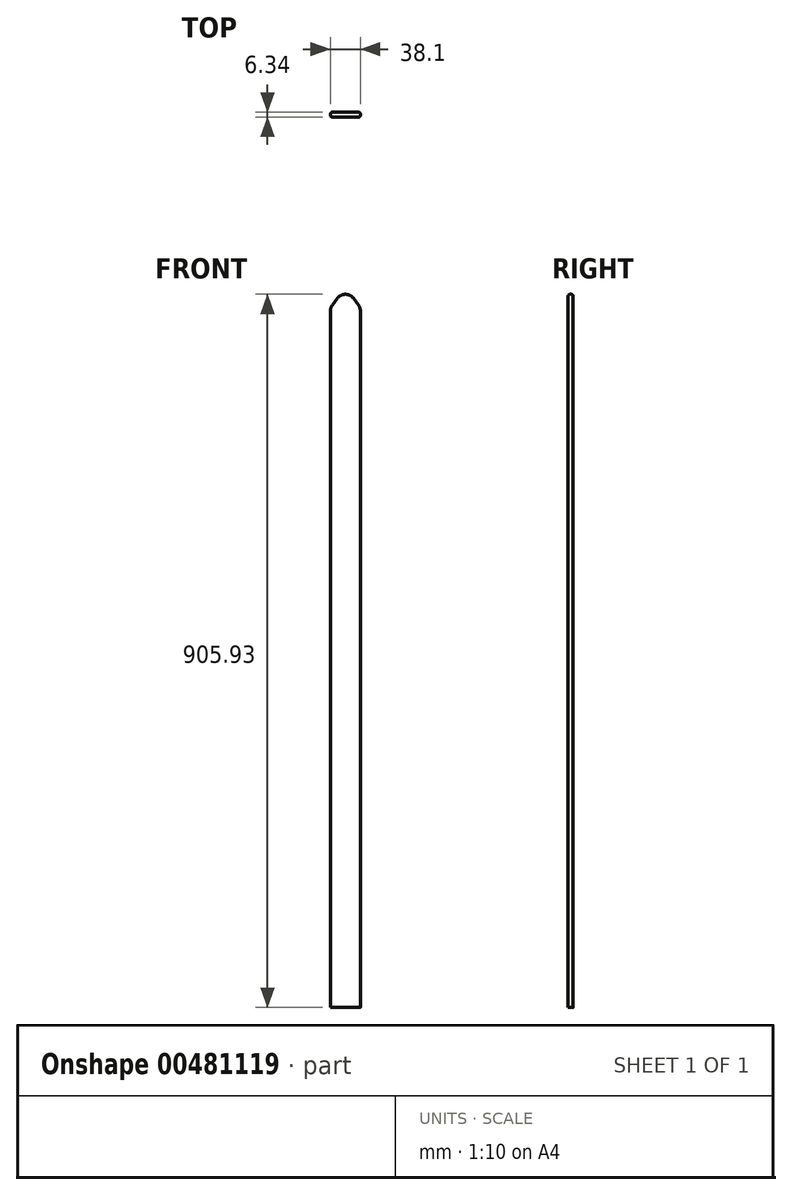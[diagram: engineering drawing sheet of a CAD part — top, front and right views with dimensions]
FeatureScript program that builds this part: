
annotation { "Feature Type Name" : "Feature", "Feature Type Description" : "" }
export const myFeature = defineFeature(function(context is Context, id is Id, definition is map)
    precondition{}
    {
        {
            var Q0;
            Q0=qCreatedBy(makeId("Front.planeOp"),FACE);
            var sketch = newSketch(context, id + "F0", { "sketchPlane" : qUnion([Q0])});
            skLineSegment(sketch, "E0", {"start": v(-19.05, 0) * mm, "end": v(-19.05, 889) * mm});
            skLineSegment(sketch, "E1", {"start": v(-19.05, 889) * mm, "end": v(0, 914.4) * mm});
            skLineSegment(sketch, "E2", {"start": v(0, 0) * mm, "end": v(0, 669.35) * mm, "construction": true});
            skLineSegment(sketch, "E3.MirrorCS", {"start": v(19.05, 889) * mm, "end": v(0, 914.4) * mm});
            skLineSegment(sketch, "E4.MirrorCS", {"start": v(19.05, 0) * mm, "end": v(19.05, 889) * mm});
            skLineSegment(sketch, "E5", {"start": v(-19.05, 0) * mm, "end": v(19.05, 0) * mm});
            skSolve(sketch);
        }
        {
            var Q0;
            Q0 = qSketchRegion(id + "F0", true);
            extrude(context, id + "F1", {"entities" : qUnion([Q0]), "endBound" : BoundingType.SYMMETRIC, "depth" : 6.35 * mm});
        }
        {
            var Q0;
            Q0=makeQuery(id+"F1.opExtrude","CAP_EDGE",EDGE,{"disambiguationData":[OSD([sQuery(id+"F0.wireOp",EDGE,"E0")])],"isStart":false});
            var Q1;
            Q1=makeQuery(id+"F1.opExtrude","CAP_EDGE",EDGE,{"disambiguationData":[OSD([sQuery(id+"F0.wireOp",EDGE,"E0")])],"isStart":true});
            var Q2;
            Q2=makeQuery(id+"F1.opExtrude","CAP_EDGE",EDGE,{"disambiguationData":[OSD([sQuery(id+"F0.wireOp",EDGE,"E1")])],"isStart":false});
            var Q3;
            Q3=makeQuery(id+"F1.opExtrude","CAP_EDGE",EDGE,{"disambiguationData":[OSD([sQuery(id+"F0.wireOp",EDGE,"E3.MirrorCS")])],"isStart":false});
            var Q4;
            Q4=makeQuery(id+"F1.opExtrude","CAP_EDGE",EDGE,{"disambiguationData":[OSD([sQuery(id+"F0.wireOp",EDGE,"E4.MirrorCS")])],"isStart":false});
            var Q5;
            Q5=makeQuery(id+"F1.opExtrude","CAP_EDGE",EDGE,{"disambiguationData":[OSD([sQuery(id+"F0.wireOp",EDGE,"E4.MirrorCS")])],"isStart":true});
            var Q6;
            Q6=makeQuery(id+"F1.opExtrude","CAP_EDGE",EDGE,{"disambiguationData":[OSD([sQuery(id+"F0.wireOp",EDGE,"E3.MirrorCS")])],"isStart":true});
            var Q7;
            Q7=makeQuery(id+"F1.opExtrude","CAP_EDGE",EDGE,{"disambiguationData":[OSD([sQuery(id+"F0.wireOp",EDGE,"E1")])],"isStart":true});
            fillet(context, id + "F2", {"entities" : qUnion([Q0, Q1, Q2, Q3, Q4, Q5, Q6, Q7]), "radius" : 2.54 * mm, "tangentPropagation" : true, "allowEdgeOverflow" : false});
        }
        {
            var Q0;
            Q0=makeQuery(id+"F2.opFillet","BLEND_EDGE",EDGE,{"blendedFrom":[makeQuery(id+"F1.opExtrude","CAP_EDGE",EDGE,{"disambiguationData":[OSD([sQuery(id+"F0.wireOp",EDGE,"E0")])],"isStart":false}),makeQuery(id+"F1.opExtrude","CAP_EDGE",EDGE,{"disambiguationData":[OSD([sQuery(id+"F0.wireOp",EDGE,"E1")])],"isStart":false})],"blendedInto":[]});
            var Q1;
            Q1=makeQuery(id+"F2.opFillet","BLEND_EDGE",EDGE,{"blendedFrom":[makeQuery(id+"F1.opExtrude","CAP_EDGE",EDGE,{"disambiguationData":[OSD([sQuery(id+"F0.wireOp",EDGE,"E1")])],"isStart":false}),makeQuery(id+"F1.opExtrude","CAP_EDGE",EDGE,{"disambiguationData":[OSD([sQuery(id+"F0.wireOp",EDGE,"E3.MirrorCS")])],"isStart":false})],"blendedInto":[]});
            var Q2;
            Q2=makeQuery(id+"F2.opFillet","BLEND_EDGE",EDGE,{"blendedFrom":[makeQuery(id+"F1.opExtrude","CAP_EDGE",EDGE,{"disambiguationData":[OSD([sQuery(id+"F0.wireOp",EDGE,"E3.MirrorCS")])],"isStart":false}),makeQuery(id+"F1.opExtrude","CAP_EDGE",EDGE,{"disambiguationData":[OSD([sQuery(id+"F0.wireOp",EDGE,"E4.MirrorCS")])],"isStart":false})],"blendedInto":[]});
            fillet(context, id + "F3", {"entities" : qUnion([Q0, Q1, Q2]), "radius" : 12.7 * mm, "tangentPropagation" : true, "allowEdgeOverflow" : false});
        }
    });
